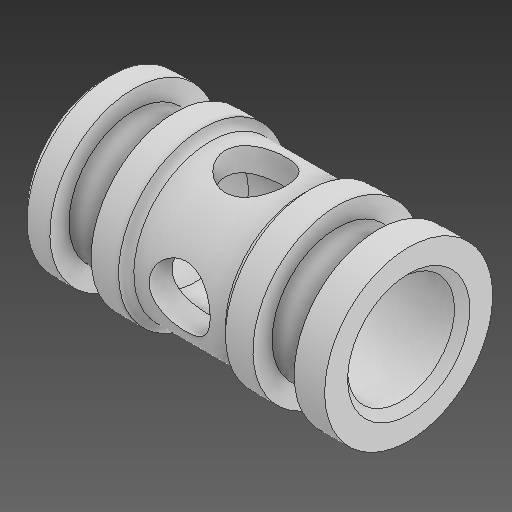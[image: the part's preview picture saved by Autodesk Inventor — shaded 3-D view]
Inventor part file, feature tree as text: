
AUTODESK INVENTOR PART (.ipt)
format: ipt  version: 2021 (Build 250183000, 183)  size: 253,952 bytes
history: native  units: in
note: dims shown in document units (in); Inventor stores cm internally (conversion verified against a paired STEP export)
features: other x3, sketch x2, plane x1
ambient origin geometry x8: Origin, YZ Plane, XZ Plane, XY Plane, X Axis, Y Axis, Z Axis, Center Point
bodies: Solid1 (feature_tree)
feature tree (6):
  other  "checkBallValve.ipt"
  other  "Solid1::checkBallValve.ipt"
  other  "TaggingFeature1"
  sketch  "Sketch2"  dims[d0=0.3937in]
  sketch  "Sketch3"
  plane  "Work Plane1"
